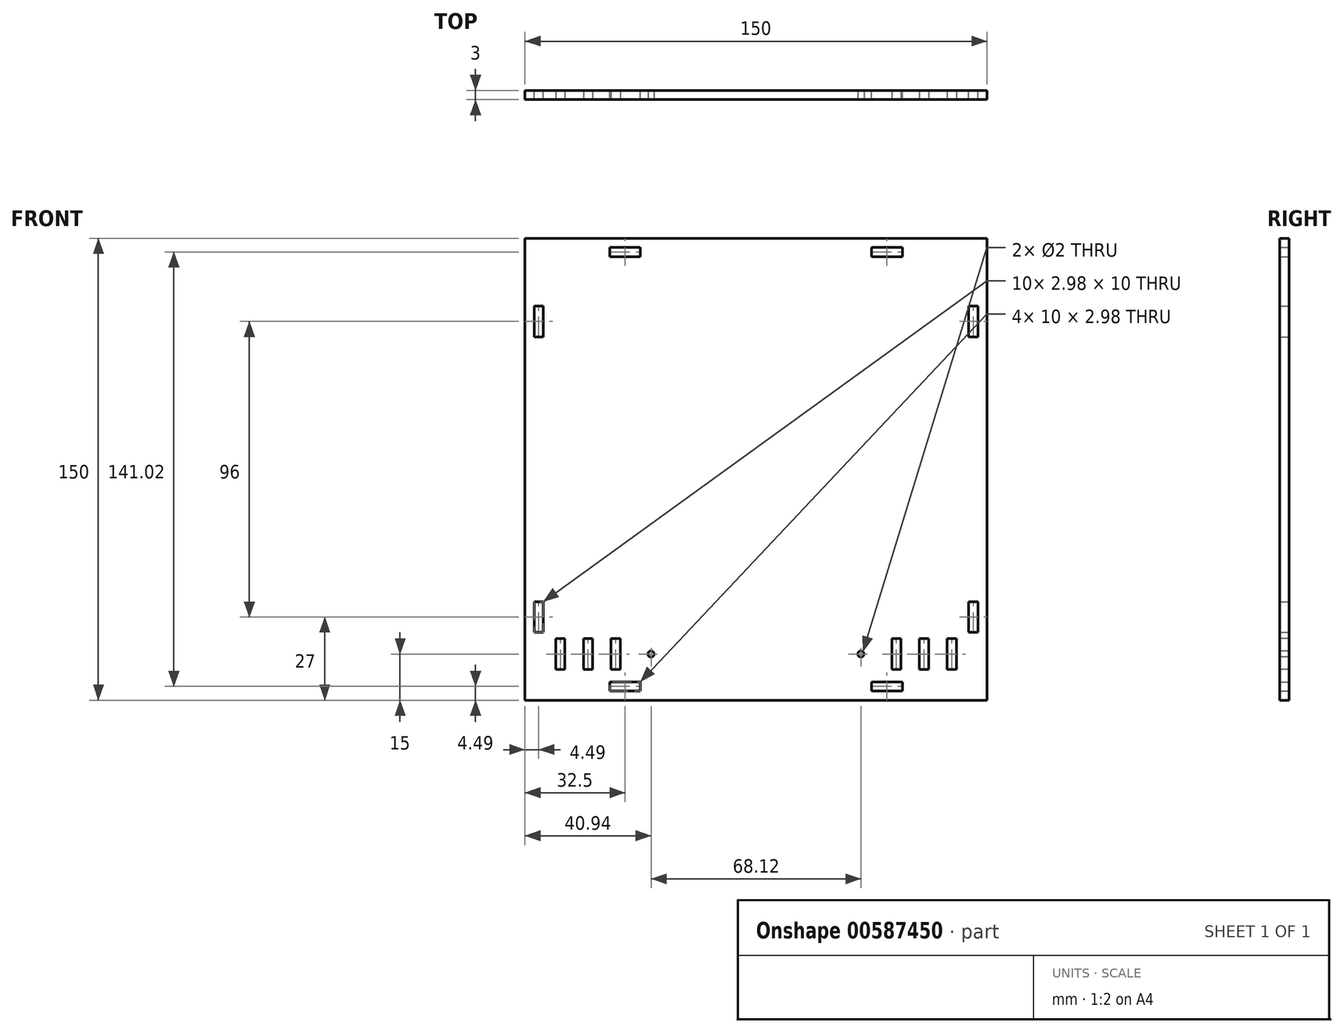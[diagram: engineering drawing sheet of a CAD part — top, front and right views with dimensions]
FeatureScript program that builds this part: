
annotation { "Feature Type Name" : "Feature", "Feature Type Description" : "" }
export const myFeature = defineFeature(function(context is Context, id is Id, definition is map)
    precondition{}
    {
        {
            var Q0;
            Q0=qCreatedBy(makeId("Front.planeOp"),FACE);
            var sketch = newSketch(context, id + "F0", { "sketchPlane" : qUnion([Q0])});
            skLineSegment(sketch, "E0.bottom", {"start": v(-75, 75) * mm, "end": v(75, 75) * mm});
            skLineSegment(sketch, "E0.top", {"start": v(-75, -75) * mm, "end": v(75, -75) * mm});
            skLineSegment(sketch, "E0.left", {"start": v(-75, 75) * mm, "end": v(-75, -75) * mm});
            skLineSegment(sketch, "E0.right", {"start": v(75, 75) * mm, "end": v(75, -75) * mm});
            skLineSegment(sketch, "E1", {"start": v(-75, 0) * mm, "end": v(75, 0) * mm, "construction": true});
            skLineSegment(sketch, "E2", {"start": v(0, 75) * mm, "end": v(0, -75) * mm, "construction": true});
            skLineSegment(sketch, "E3.bottom", {"start": v(-47.5, 72) * mm, "end": v(-37.5, 72) * mm});
            skLineSegment(sketch, "E3.top", {"start": v(-47.5, 69.02) * mm, "end": v(-37.5, 69.02) * mm});
            skLineSegment(sketch, "E3.left", {"start": v(-47.5, 72) * mm, "end": v(-47.5, 69.02) * mm});
            skLineSegment(sketch, "E3.right", {"start": v(-37.5, 72) * mm, "end": v(-37.5, 69.02) * mm});
            skLineSegment(sketch, "E4", {"start": v(-42.5, 72) * mm, "end": v(-42.5, 69.02) * mm, "construction": true});
            skLineSegment(sketch, "E5", {"start": v(-47.5, 70.5) * mm, "end": v(-37.5, 70.5) * mm, "construction": true});
            skLineSegment(sketch, "E6.MirrorCS", {"start": v(37.5, 72) * mm, "end": v(37.5, 69.02) * mm});
            skLineSegment(sketch, "E7.MirrorCS", {"start": v(47.5, 72) * mm, "end": v(47.5, 69.02) * mm});
            skLineSegment(sketch, "E8.MirrorCS", {"start": v(47.5, 72) * mm, "end": v(37.5, 72) * mm});
            skLineSegment(sketch, "E9.MirrorCS", {"start": v(42.5, 72) * mm, "end": v(42.5, 69.02) * mm, "construction": true});
            skLineSegment(sketch, "E10.MirrorCS", {"start": v(47.5, 69.02) * mm, "end": v(37.5, 69.02) * mm});
            skLineSegment(sketch, "E11.MirrorCS", {"start": v(47.5, 70.5) * mm, "end": v(37.5, 70.5) * mm, "construction": true});
            skLineSegment(sketch, "E12.MirrorCS", {"start": v(47.5, -72) * mm, "end": v(37.5, -72) * mm});
            skLineSegment(sketch, "E13.MirrorCS", {"start": v(47.5, -72) * mm, "end": v(47.5, -69.02) * mm});
            skLineSegment(sketch, "E14.MirrorCS", {"start": v(47.5, -69.02) * mm, "end": v(37.5, -69.02) * mm});
            skLineSegment(sketch, "E15.MirrorCS", {"start": v(47.5, -70.51) * mm, "end": v(37.5, -70.51) * mm, "construction": true});
            skLineSegment(sketch, "E16.MirrorCS", {"start": v(37.5, -72) * mm, "end": v(37.5, -69.02) * mm});
            skLineSegment(sketch, "E17.MirrorCS", {"start": v(42.5, -72) * mm, "end": v(42.5, -69.02) * mm, "construction": true});
            skLineSegment(sketch, "E18.MirrorCS", {"start": v(-37.5, -72) * mm, "end": v(-37.5, -69.02) * mm});
            skLineSegment(sketch, "E19.MirrorCS", {"start": v(-47.5, -72) * mm, "end": v(-47.5, -69.02) * mm});
            skLineSegment(sketch, "E20.MirrorCS", {"start": v(-47.5, -70.51) * mm, "end": v(-37.5, -70.51) * mm, "construction": true});
            skLineSegment(sketch, "E21.MirrorCS", {"start": v(-47.5, -69.02) * mm, "end": v(-37.5, -69.02) * mm});
            skLineSegment(sketch, "E22.MirrorCS", {"start": v(-42.5, -72) * mm, "end": v(-42.5, -69.02) * mm, "construction": true});
            skLineSegment(sketch, "E23.MirrorCS", {"start": v(-47.5, -72) * mm, "end": v(-37.5, -72) * mm});
            skLineSegment(sketch, "E24.bottom", {"start": v(-72, 53) * mm, "end": v(-69.02, 53) * mm});
            skLineSegment(sketch, "E24.top", {"start": v(-72, 43) * mm, "end": v(-69.02, 43) * mm});
            skLineSegment(sketch, "E24.left", {"start": v(-72, 53) * mm, "end": v(-72, 43) * mm});
            skLineSegment(sketch, "E24.right", {"start": v(-69.02, 53) * mm, "end": v(-69.02, 43) * mm});
            skLineSegment(sketch, "E25", {"start": v(-70.5, 53) * mm, "end": v(-70.5, 43) * mm, "construction": true});
            skLineSegment(sketch, "E26", {"start": v(-72, 48) * mm, "end": v(-69.02, 48) * mm, "construction": true});
            skLineSegment(sketch, "E27.MirrorCS", {"start": v(72, 53) * mm, "end": v(69.02, 53) * mm});
            skLineSegment(sketch, "E28.MirrorCS", {"start": v(72, 43) * mm, "end": v(69.02, 43) * mm});
            skLineSegment(sketch, "E29.MirrorCS", {"start": v(69.02, 53) * mm, "end": v(69.02, 43) * mm});
            skLineSegment(sketch, "E30.MirrorCS", {"start": v(72, 48) * mm, "end": v(69.02, 48) * mm, "construction": true});
            skLineSegment(sketch, "E31.MirrorCS", {"start": v(72, 53) * mm, "end": v(72, 43) * mm});
            skLineSegment(sketch, "E32.MirrorCS", {"start": v(70.5, 53) * mm, "end": v(70.5, 43) * mm, "construction": true});
            skLineSegment(sketch, "E33.MirrorCS", {"start": v(72, -43) * mm, "end": v(69.02, -43) * mm});
            skLineSegment(sketch, "E34.MirrorCS", {"start": v(72, -53) * mm, "end": v(69.02, -53) * mm});
            skLineSegment(sketch, "E35.MirrorCS", {"start": v(69.02, -53) * mm, "end": v(69.02, -43) * mm});
            skLineSegment(sketch, "E36.MirrorCS", {"start": v(72, -48) * mm, "end": v(69.02, -48) * mm, "construction": true});
            skLineSegment(sketch, "E37.MirrorCS", {"start": v(72, -53) * mm, "end": v(72, -43) * mm});
            skLineSegment(sketch, "E38.MirrorCS", {"start": v(70.5, -53) * mm, "end": v(70.5, -43) * mm, "construction": true});
            skLineSegment(sketch, "E39.MirrorCS", {"start": v(-72, -53) * mm, "end": v(-72, -43) * mm});
            skLineSegment(sketch, "E40.MirrorCS", {"start": v(-72, -48) * mm, "end": v(-69.02, -48) * mm, "construction": true});
            skLineSegment(sketch, "E41.MirrorCS", {"start": v(-70.5, -53) * mm, "end": v(-70.5, -43) * mm, "construction": true});
            skLineSegment(sketch, "E42.MirrorCS", {"start": v(-72, -53) * mm, "end": v(-69.02, -53) * mm});
            skLineSegment(sketch, "E43.MirrorCS", {"start": v(-72, -43) * mm, "end": v(-69.02, -43) * mm});
            skLineSegment(sketch, "E44.MirrorCS", {"start": v(-69.02, -53) * mm, "end": v(-69.02, -43) * mm});
            skLineSegment(sketch, "E45.bottom", {"start": v(-71.49, 5.01) * mm, "end": v(-68.51, 5.01) * mm});
            skLineSegment(sketch, "E45.top", {"start": v(-71.49, -4.99) * mm, "end": v(-68.51, -4.99) * mm});
            skLineSegment(sketch, "E45.left", {"start": v(-71.49, 5.01) * mm, "end": v(-71.49, -4.99) * mm});
            skLineSegment(sketch, "E46", {"start": v(-70, 5.01) * mm, "end": v(-70, -4.99) * mm, "construction": true});
            skLineSegment(sketch, "E47", {"start": v(-71.49, 0.01) * mm, "end": v(-68.51, 0.01) * mm, "construction": true});
            skLineSegment(sketch, "E48.1.0.0", {"start": v(-61.49, 0.01) * mm, "end": v(-58.51, 0.01) * mm, "construction": true});
            skLineSegment(sketch, "E48.1.0.2", {"start": v(-61.49, 5.01) * mm, "end": v(-61.49, -4.99) * mm});
            skLineSegment(sketch, "E48.1.0.3", {"start": v(-60, 5.01) * mm, "end": v(-60, -4.99) * mm, "construction": true});
            skLineSegment(sketch, "E48.1.0.4", {"start": v(-61.49, 5.01) * mm, "end": v(-58.51, 5.01) * mm});
            skLineSegment(sketch, "E48.1.0.5", {"start": v(-61.49, -4.99) * mm, "end": v(-58.51, -4.99) * mm});
            skLineSegment(sketch, "E48.2.0.0", {"start": v(-51.49, 0.01) * mm, "end": v(-48.51, 0.01) * mm, "construction": true});
            skLineSegment(sketch, "E48.2.0.2", {"start": v(-51.49, 5.01) * mm, "end": v(-51.49, -4.99) * mm});
            skLineSegment(sketch, "E48.2.0.3", {"start": v(-50, 5.01) * mm, "end": v(-50, -4.99) * mm, "construction": true});
            skLineSegment(sketch, "E48.2.0.4", {"start": v(-51.49, 5.01) * mm, "end": v(-48.51, 5.01) * mm});
            skLineSegment(sketch, "E48.2.0.5", {"start": v(-51.49, -4.99) * mm, "end": v(-48.51, -4.99) * mm});
            skLineSegment(sketch, "E48.direction1", {"start": v(-71.49, -4.99) * mm, "end": v(-61.49, -4.99) * mm, "construction": true});
            skLineSegment(sketch, "E49.MirrorCS", {"start": v(61.5, -4.99) * mm, "end": v(58.51, -4.99) * mm});
            skLineSegment(sketch, "E50.MirrorCS", {"start": v(51.5, -4.99) * mm, "end": v(48.51, -4.99) * mm});
            skLineSegment(sketch, "E51.MirrorCS", {"start": v(71.49, 5.01) * mm, "end": v(68.51, 5.01) * mm});
            skLineSegment(sketch, "E52.MirrorCS", {"start": v(71.49, -4.99) * mm, "end": v(68.51, -4.99) * mm});
            skLineSegment(sketch, "E53.MirrorCS", {"start": v(61.5, 0.01) * mm, "end": v(58.51, 0.01) * mm, "construction": true});
            skLineSegment(sketch, "E54.MirrorCS", {"start": v(51.5, 0.01) * mm, "end": v(48.51, 0.01) * mm, "construction": true});
            skLineSegment(sketch, "E55.MirrorCS", {"start": v(50, 5.01) * mm, "end": v(50, -4.99) * mm, "construction": true});
            skLineSegment(sketch, "E56.MirrorCS", {"start": v(58.51, 5.01) * mm, "end": v(58.51, -4.99) * mm});
            skLineSegment(sketch, "E57.MirrorCS", {"start": v(71.49, 0.01) * mm, "end": v(68.51, 0.01) * mm, "construction": true});
            skLineSegment(sketch, "E58.MirrorCS", {"start": v(71.49, -4.99) * mm, "end": v(61.5, -4.99) * mm, "construction": true});
            skLineSegment(sketch, "E59.MirrorCS", {"start": v(60, 5.01) * mm, "end": v(60, -4.99) * mm, "construction": true});
            skLineSegment(sketch, "E60.MirrorCS", {"start": v(70, 5.01) * mm, "end": v(70, -4.99) * mm, "construction": true});
            skLineSegment(sketch, "E61.MirrorCS", {"start": v(71.5, 5.01) * mm, "end": v(71.5, -4.99) * mm});
            skLineSegment(sketch, "E62.MirrorCS", {"start": v(48.51, 5.01) * mm, "end": v(48.51, -4.99) * mm});
            skLineSegment(sketch, "E63.MirrorCS", {"start": v(75, 0) * mm, "end": v(-75, 0) * mm, "construction": true});
            skLineSegment(sketch, "E64.MirrorCS", {"start": v(51.5, 5.01) * mm, "end": v(51.5, -4.99) * mm});
            skLineSegment(sketch, "E65.MirrorCS", {"start": v(61.5, 5.01) * mm, "end": v(61.5, -4.99) * mm});
            skSolve(sketch);
        }
        {
            var Q0;
            Q0 = qSketchRegion(id + "F0", true);
            extrude(context, id + "F1", {"entities" : qUnion([Q0]), "depth" : 3 * mm, "offsetDistance" : 25 * mm});
        }
        {
            var Q0;
            Q0=makeQuery(id+"F1.opExtrude","CAP_FACE",FACE,{"disambiguationData":[OSD([sQuery(id+"F0.wireOp",EDGE,"E0.bottom"),sQuery(id+"F0.wireOp",EDGE,"E0.top"),sQuery(id+"F0.wireOp",EDGE,"E0.left"),sQuery(id+"F0.wireOp",EDGE,"E0.right"),sQuery(id+"F0.wireOp",EDGE,"E3.bottom"),sQuery(id+"F0.wireOp",EDGE,"E3.top"),sQuery(id+"F0.wireOp",EDGE,"E3.left"),sQuery(id+"F0.wireOp",EDGE,"E3.right"),sQuery(id+"F0.wireOp",EDGE,"E6.MirrorCS"),sQuery(id+"F0.wireOp",EDGE,"E7.MirrorCS"),sQuery(id+"F0.wireOp",EDGE,"E8.MirrorCS"),sQuery(id+"F0.wireOp",EDGE,"E10.MirrorCS"),sQuery(id+"F0.wireOp",EDGE,"E12.MirrorCS"),sQuery(id+"F0.wireOp",EDGE,"E13.MirrorCS"),sQuery(id+"F0.wireOp",EDGE,"E14.MirrorCS"),sQuery(id+"F0.wireOp",EDGE,"E16.MirrorCS"),sQuery(id+"F0.wireOp",EDGE,"E18.MirrorCS"),sQuery(id+"F0.wireOp",EDGE,"E19.MirrorCS"),sQuery(id+"F0.wireOp",EDGE,"E21.MirrorCS"),sQuery(id+"F0.wireOp",EDGE,"E23.MirrorCS"),sQuery(id+"F0.wireOp",EDGE,"E24.bottom"),sQuery(id+"F0.wireOp",EDGE,"E24.top"),sQuery(id+"F0.wireOp",EDGE,"E24.left"),sQuery(id+"F0.wireOp",EDGE,"E24.right"),sQuery(id+"F0.wireOp",EDGE,"E27.MirrorCS"),sQuery(id+"F0.wireOp",EDGE,"E28.MirrorCS"),sQuery(id+"F0.wireOp",EDGE,"E29.MirrorCS"),sQuery(id+"F0.wireOp",EDGE,"E31.MirrorCS"),sQuery(id+"F0.wireOp",EDGE,"E33.MirrorCS"),sQuery(id+"F0.wireOp",EDGE,"E34.MirrorCS"),sQuery(id+"F0.wireOp",EDGE,"E35.MirrorCS"),sQuery(id+"F0.wireOp",EDGE,"E37.MirrorCS"),sQuery(id+"F0.wireOp",EDGE,"E39.MirrorCS"),sQuery(id+"F0.wireOp",EDGE,"E42.MirrorCS"),sQuery(id+"F0.wireOp",EDGE,"E43.MirrorCS"),sQuery(id+"F0.wireOp",EDGE,"E44.MirrorCS")])],"isStart":false});
            var sketch = newSketch(context, id + "F2", { "sketchPlane" : qUnion([Q0])});
            skLineSegment(sketch, "E66.bottom", {"start": v(-62.02, -55) * mm, "end": v(-65, -55) * mm});
            skLineSegment(sketch, "E66.top", {"start": v(-62.02, -65) * mm, "end": v(-65, -65) * mm});
            skLineSegment(sketch, "E66.left", {"start": v(-62.02, -55) * mm, "end": v(-62.02, -65) * mm});
            skLineSegment(sketch, "E66.right", {"start": v(-65, -55) * mm, "end": v(-65, -65) * mm});
            skPoint(sketch, "E66.middle", {"position": v(-63.51, -60) * mm});
            skLineSegment(sketch, "E67.bottom", {"start": v(-44.06, -55) * mm, "end": v(-47.04, -55) * mm});
            skLineSegment(sketch, "E67.top", {"start": v(-44.06, -65) * mm, "end": v(-47.04, -65) * mm});
            skLineSegment(sketch, "E67.left", {"start": v(-44.06, -55) * mm, "end": v(-44.06, -65) * mm});
            skLineSegment(sketch, "E67.right", {"start": v(-47.04, -55) * mm, "end": v(-47.04, -65) * mm});
            skPoint(sketch, "E67.middle", {"position": v(-54.53, -60) * mm});
            skLineSegment(sketch, "E68.bottom", {"start": v(-56.02, -55) * mm, "end": v(-53.04, -55) * mm});
            skLineSegment(sketch, "E68.top", {"start": v(-56.02, -65) * mm, "end": v(-53.04, -65) * mm});
            skLineSegment(sketch, "E68.left", {"start": v(-56.02, -55) * mm, "end": v(-56.02, -65) * mm});
            skLineSegment(sketch, "E68.right", {"start": v(-53.04, -55) * mm, "end": v(-53.04, -65) * mm});
            skCircle(sketch, "E69", {"center": v(-34.06, -60) * mm, "radius": 1 * mm});
            skLineSegment(sketch, "E70", {"start": v(-63.5, -60) * mm, "end": v(-4.1, -60) * mm});
            skPoint(sketch, "E70.endSnap0", {"position": v(-62.02, -60) * mm});
            skPoint(sketch, "E71", {"position": v(-44.06, -60) * mm});
            skLineSegment(sketch, "E72", {"start": v(0, 75) * mm, "end": v(0, 48.77) * mm});
            skPoint(sketch, "E72.endSnap0", {"position": v(0, 75) * mm});
            skCircle(sketch, "E73.MirrorC", {"center": v(34.06, -60) * mm, "radius": 1 * mm});
            skLineSegment(sketch, "E74.MirrorCS", {"start": v(44.06, -55) * mm, "end": v(44.06, -65) * mm});
            skLineSegment(sketch, "E75.MirrorCS", {"start": v(44.06, -55) * mm, "end": v(47.04, -55) * mm});
            skPoint(sketch, "E76.MirrorP", {"position": v(54.53, -60) * mm});
            skLineSegment(sketch, "E77.MirrorCS", {"start": v(47.04, -55) * mm, "end": v(47.04, -65) * mm});
            skLineSegment(sketch, "E78.MirrorCS", {"start": v(65, -55) * mm, "end": v(65, -65) * mm});
            skLineSegment(sketch, "E79.MirrorCS", {"start": v(53.04, -55) * mm, "end": v(53.04, -65) * mm});
            skLineSegment(sketch, "E80.MirrorCS", {"start": v(56.02, -55) * mm, "end": v(56.02, -65) * mm});
            skLineSegment(sketch, "E81.MirrorCS", {"start": v(62.02, -55) * mm, "end": v(65, -55) * mm});
            skLineSegment(sketch, "E82.MirrorCS", {"start": v(62.02, -55) * mm, "end": v(62.02, -65) * mm});
            skLineSegment(sketch, "E83.MirrorCS", {"start": v(62.02, -65) * mm, "end": v(65, -65) * mm});
            skPoint(sketch, "E84.MirrorP", {"position": v(62.02, -60) * mm});
            skPoint(sketch, "E85.MirrorP", {"position": v(63.5, -60) * mm});
            skLineSegment(sketch, "E86.MirrorCS", {"start": v(56.02, -55) * mm, "end": v(53.04, -55) * mm});
            skLineSegment(sketch, "E87.MirrorCS", {"start": v(56.02, -65) * mm, "end": v(53.04, -65) * mm});
            skLineSegment(sketch, "E88.MirrorCS", {"start": v(44.06, -65) * mm, "end": v(47.04, -65) * mm});
            skPoint(sketch, "E89.MirrorP", {"position": v(44.06, -60) * mm});
            skSolve(sketch);
        }
        {
            var Q0;
            Q0 = qSketchRegion(id + "F2", true);
            extrude(context, id + "F3", {"entities" : qUnion([Q0]), "operationType" : NewBodyOperationType.REMOVE, "oppositeDirection" : true, "depth" : 3 * mm, "offsetDistance" : 25 * mm});
        }
    });
